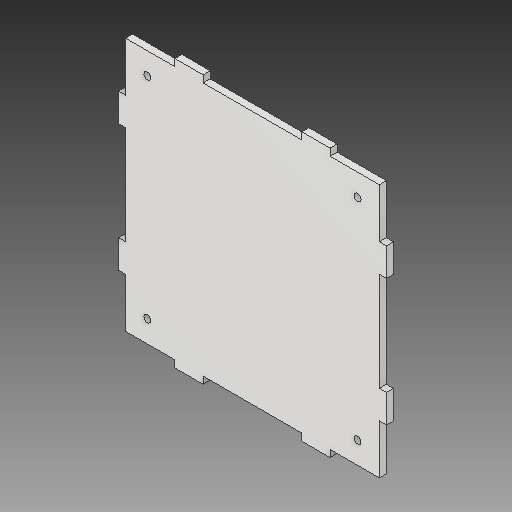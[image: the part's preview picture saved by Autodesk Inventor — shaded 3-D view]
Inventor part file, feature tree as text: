
AUTODESK INVENTOR PART (.ipt)
format: ipt  version: 2018.2 (Build 222227000, 227)  size: 126,464 bytes
history: native  units: in
note: dims shown in document units (in); Inventor stores cm internally (conversion verified against a paired STEP export)
features: reference x4, other x4, extrude x1, sketch x1
ambient origin geometry x8: Origin, YZ Plane, XZ Plane, XY Plane, X Axis, Y Axis, Z Axis, Center Point
bodies: Solid1 (feature_tree)
feature tree (10):
  extrude  "Extrusion1"  [1 undecoded]
  sketch  "Sketch1"  dims[d0=0.125in d1=0.0in]
  reference  "Reference2"
  reference  "Reference3"
  reference  "Reference4"
  reference  "Reference5"
  other  "Assembly1.iam"
  other  "Finger Print Scanner v5:1"
  other  "PCB Component:1"
  other  "Board:1"
note: 1 required parameter value undecoded (feature->parameter linkage not recoverable at this tier; creation-order binding heuristic only, values carry confidence <= 0.55)
